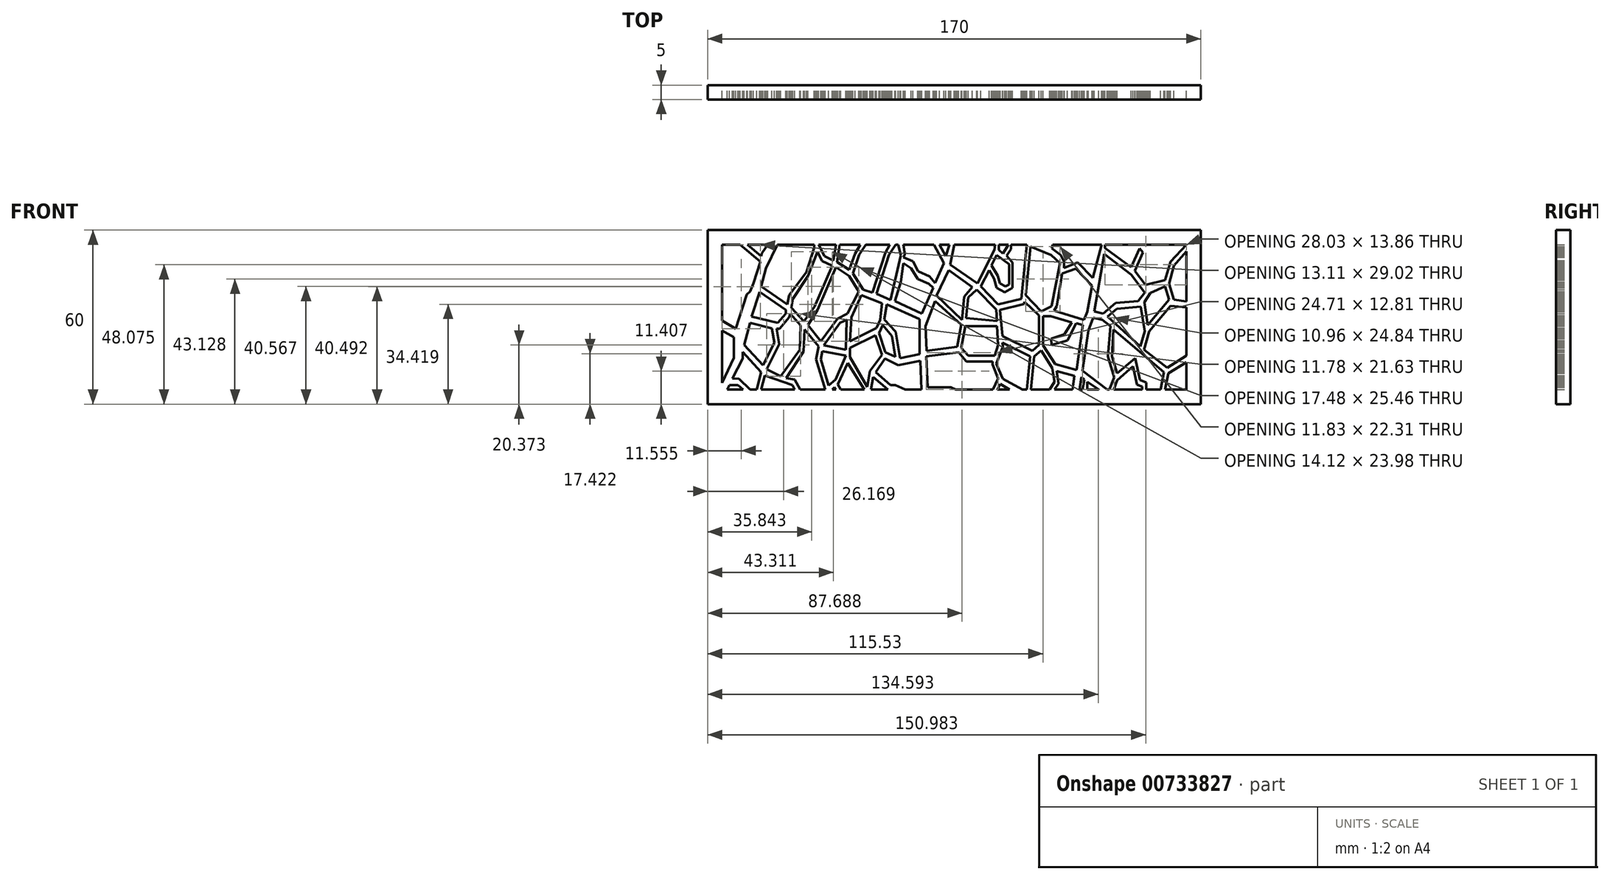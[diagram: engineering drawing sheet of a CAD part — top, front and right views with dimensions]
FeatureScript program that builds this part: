
annotation { "Feature Type Name" : "Feature", "Feature Type Description" : "" }
export const myFeature = defineFeature(function(context is Context, id is Id, definition is map)
    precondition{}
    {
        {
            var Q0;
            Q0=qCreatedBy(makeId("Front.planeOp"),FACE);
            var sketch = newSketch(context, id + "F0", { "sketchPlane" : qUnion([Q0])});
            skLineSegment(sketch, "E0.0", {"start": v(-29.57, -53.65) * mm, "end": v(130.43, -53.65) * mm});
            skLineSegment(sketch, "E0.1", {"start": v(-29.57, -103.65) * mm, "end": v(-29.57, -53.65) * mm});
            skLineSegment(sketch, "E0.2", {"start": v(130.43, -103.65) * mm, "end": v(-29.57, -103.65) * mm});
            skLineSegment(sketch, "E0.3", {"start": v(130.43, -103.65) * mm, "end": v(130.43, -53.65) * mm});
            skLineSegment(sketch, "E1", {"start": v(-29.57, -101.33) * mm, "end": v(-25.59, -92.68) * mm});
            skLineSegment(sketch, "E2", {"start": v(-25.59, -92.68) * mm, "end": v(-25.59, -85.56) * mm});
            skLineSegment(sketch, "E3", {"start": v(-25.59, -85.56) * mm, "end": v(-29.57, -83.34) * mm});
            skLineSegment(sketch, "E4", {"start": v(-27.87, -103.65) * mm, "end": v(-27.12, -102.02) * mm});
            skLineSegment(sketch, "E5", {"start": v(-27.12, -102.02) * mm, "end": v(-24.2, -102.02) * mm});
            skLineSegment(sketch, "E6", {"start": v(-24.2, -102.02) * mm, "end": v(-22.4, -103.65) * mm});
            skLineSegment(sketch, "E7", {"start": v(-26.07, -99.81) * mm, "end": v(-22.54, -92.9) * mm});
            skLineSegment(sketch, "E8", {"start": v(-22.54, -92.9) * mm, "end": v(-22.54, -90.6) * mm});
            skLineSegment(sketch, "E9", {"start": v(-22.54, -90.6) * mm, "end": v(-16.1, -97.6) * mm});
            skLineSegment(sketch, "E10", {"start": v(-16.1, -97.6) * mm, "end": v(-17.63, -103.65) * mm});
            skLineSegment(sketch, "E11", {"start": v(-19.91, -103.65) * mm, "end": v(-23.79, -99.88) * mm});
            skLineSegment(sketch, "E12", {"start": v(-23.79, -99.88) * mm, "end": v(-26.07, -99.81) * mm});
            skLineSegment(sketch, "E13", {"start": v(-22, -88.19) * mm, "end": v(-15.52, -95.21) * mm});
            skLineSegment(sketch, "E14", {"start": v(-15.52, -95.21) * mm, "end": v(-11.6, -87.53) * mm});
            skLineSegment(sketch, "E15", {"start": v(-11.6, -87.53) * mm, "end": v(-12.44, -82.51) * mm});
            skLineSegment(sketch, "E16", {"start": v(-12.44, -82.51) * mm, "end": v(-19.93, -80.63) * mm});
            skLineSegment(sketch, "E17", {"start": v(-19.93, -80.63) * mm, "end": v(-22, -88.19) * mm});
            skLineSegment(sketch, "E18", {"start": v(-16.1, -103.65) * mm, "end": v(-14.88, -98.77) * mm});
            skLineSegment(sketch, "E19", {"start": v(-14.88, -98.77) * mm, "end": v(-5.32, -102.02) * mm});
            skLineSegment(sketch, "E20", {"start": v(-5.32, -102.02) * mm, "end": v(-4.55, -103.65) * mm});
            skLineSegment(sketch, "E21", {"start": v(-6.15, -77.46) * mm, "end": v(-6.49, -78.68) * mm});
            skLineSegment(sketch, "E22", {"start": v(-6.49, -78.68) * mm, "end": v(-9.86, -82.67) * mm});
            skLineSegment(sketch, "E23", {"start": v(-9.86, -82.67) * mm, "end": v(-10.82, -82.67) * mm});
            skLineSegment(sketch, "E24", {"start": v(-10.82, -82.67) * mm, "end": v(-9.92, -87.93) * mm});
            skLineSegment(sketch, "E25", {"start": v(-9.92, -87.93) * mm, "end": v(-14.3, -96.68) * mm});
            skLineSegment(sketch, "E26", {"start": v(-14.3, -96.68) * mm, "end": v(-9.46, -99.1) * mm});
            skLineSegment(sketch, "E27", {"start": v(-9.46, -99.1) * mm, "end": v(-2.8, -89.9) * mm});
            skLineSegment(sketch, "E28", {"start": v(-2.8, -89.9) * mm, "end": v(-2.51, -81.56) * mm});
            skLineSegment(sketch, "E29", {"start": v(-2.51, -81.56) * mm, "end": v(-6.15, -77.46) * mm});
            skLineSegment(sketch, "E30", {"start": v(-1.11, -82.9) * mm, "end": v(3.69, -88.68) * mm});
            skLineSegment(sketch, "E31", {"start": v(3.69, -88.68) * mm, "end": v(2.81, -93.2) * mm});
            skLineSegment(sketch, "E32", {"start": v(2.81, -93.2) * mm, "end": v(5.94, -103.65) * mm});
            skLineSegment(sketch, "E33", {"start": v(-2.66, -103.65) * mm, "end": v(-4.6, -100.21) * mm});
            skLineSegment(sketch, "E34", {"start": v(-4.6, -100.21) * mm, "end": v(-7.51, -99.68) * mm});
            skLineSegment(sketch, "E35", {"start": v(-7.51, -99.68) * mm, "end": v(-1.53, -90.55) * mm});
            skLineSegment(sketch, "E36", {"start": v(-1.53, -90.55) * mm, "end": v(-1.11, -82.9) * mm});
            skLineSegment(sketch, "E37", {"start": v(7.09, -102.26) * mm, "end": v(4.38, -93.18) * mm});
            skPoint(sketch, "E37.endSnap0", {"position": v(4.38, -98.42) * mm});
            skLineSegment(sketch, "E38", {"start": v(4.38, -93.18) * mm, "end": v(4.9, -90.4) * mm});
            skLineSegment(sketch, "E39", {"start": v(4.9, -90.4) * mm, "end": v(13.02, -91.96) * mm});
            skLineSegment(sketch, "E40", {"start": v(13.02, -91.96) * mm, "end": v(9.52, -100.16) * mm});
            skLineSegment(sketch, "E41", {"start": v(9.52, -100.16) * mm, "end": v(7.09, -102.26) * mm});
            skLineSegment(sketch, "E42", {"start": v(8.3, -103.65) * mm, "end": v(9.16, -102.9) * mm});
            skPoint(sketch, "E42.startSnap0", {"position": v(8.3, -101.2) * mm});
            skLineSegment(sketch, "E43", {"start": v(9.16, -102.9) * mm, "end": v(9.58, -103.65) * mm});
            skLineSegment(sketch, "E44", {"start": v(11.34, -103.65) * mm, "end": v(10.29, -101.83) * mm});
            skLineSegment(sketch, "E45", {"start": v(10.29, -101.83) * mm, "end": v(13.64, -94.5) * mm});
            skLineSegment(sketch, "E46", {"start": v(13.64, -94.5) * mm, "end": v(19.36, -103.65) * mm});
            skLineSegment(sketch, "E47", {"start": v(20.49, -102.69) * mm, "end": v(14.45, -92.42) * mm});
            skLineSegment(sketch, "E48", {"start": v(14.45, -92.42) * mm, "end": v(14.45, -89.3) * mm});
            skLineSegment(sketch, "E49", {"start": v(14.45, -89.3) * mm, "end": v(23.18, -84.96) * mm});
            skLineSegment(sketch, "E50", {"start": v(23.18, -84.96) * mm, "end": v(25.5, -91.66) * mm});
            skLineSegment(sketch, "E51", {"start": v(25.5, -91.66) * mm, "end": v(21.32, -97.28) * mm});
            skLineSegment(sketch, "E52", {"start": v(21.32, -97.28) * mm, "end": v(20.49, -102.69) * mm});
            skLineSegment(sketch, "E53", {"start": v(5.46, -88.33) * mm, "end": v(13.07, -89.85) * mm});
            skLineSegment(sketch, "E54", {"start": v(13.07, -89.85) * mm, "end": v(13.29, -79.56) * mm});
            skLineSegment(sketch, "E55", {"start": v(13.29, -79.56) * mm, "end": v(11.06, -80.67) * mm});
            skLineSegment(sketch, "E56", {"start": v(11.06, -80.67) * mm, "end": v(5.46, -88.33) * mm});
            skLineSegment(sketch, "E57", {"start": v(4.44, -86.96) * mm, "end": v(10.14, -79.16) * mm});
            skLineSegment(sketch, "E58", {"start": v(10.14, -79.16) * mm, "end": v(13.59, -77.44) * mm});
            skLineSegment(sketch, "E59", {"start": v(13.59, -77.44) * mm, "end": v(17.48, -69.77) * mm});
            skLineSegment(sketch, "E60", {"start": v(17.48, -69.77) * mm, "end": v(14.17, -64.47) * mm});
            skLineSegment(sketch, "E61", {"start": v(14.17, -64.47) * mm, "end": v(9.65, -61.5) * mm});
            skLineSegment(sketch, "E62", {"start": v(9.65, -61.5) * mm, "end": v(3.33, -76.24) * mm});
            skLineSegment(sketch, "E63", {"start": v(3.33, -76.24) * mm, "end": v(0, -81.32) * mm});
            skLineSegment(sketch, "E64", {"start": v(0, -81.32) * mm, "end": v(4.44, -86.96) * mm});
            skLineSegment(sketch, "E65", {"start": v(14.45, -86.96) * mm, "end": v(23.64, -82.38) * mm});
            skLineSegment(sketch, "E66", {"start": v(23.64, -82.38) * mm, "end": v(24.92, -79.56) * mm});
            skLineSegment(sketch, "E67", {"start": v(24.92, -79.56) * mm, "end": v(25.5, -73.83) * mm});
            skLineSegment(sketch, "E68", {"start": v(25.5, -73.83) * mm, "end": v(18.42, -71.1) * mm});
            skLineSegment(sketch, "E69", {"start": v(18.42, -71.1) * mm, "end": v(14.94, -78.72) * mm});
            skLineSegment(sketch, "E70", {"start": v(14.94, -78.72) * mm, "end": v(14.45, -86.96) * mm});
            skLineSegment(sketch, "E71", {"start": v(8.33, -60.96) * mm, "end": v(2.29, -75.06) * mm});
            skLineSegment(sketch, "E72", {"start": v(2.29, -75.06) * mm, "end": v(-1.37, -80.07) * mm});
            skLineSegment(sketch, "E73", {"start": v(-1.37, -80.07) * mm, "end": v(-5.79, -75.45) * mm});
            skLineSegment(sketch, "E74", {"start": v(-5.79, -75.45) * mm, "end": v(-5.16, -72.34) * mm});
            skLineSegment(sketch, "E75", {"start": v(-5.16, -72.34) * mm, "end": v(0, -64.46) * mm});
            skLineSegment(sketch, "E76", {"start": v(0, -64.46) * mm, "end": v(3.23, -56.1) * mm});
            skLineSegment(sketch, "E77", {"start": v(3.23, -56.1) * mm, "end": v(4.8, -59.26) * mm});
            skLineSegment(sketch, "E78", {"start": v(4.8, -59.26) * mm, "end": v(8.33, -60.96) * mm});
            skLineSegment(sketch, "E79", {"start": v(-19.43, -78.5) * mm, "end": v(-10.37, -80.67) * mm});
            skLineSegment(sketch, "E80", {"start": v(-10.37, -80.67) * mm, "end": v(-7.66, -77.46) * mm});
            skLineSegment(sketch, "E81", {"start": v(-7.66, -77.46) * mm, "end": v(-7.66, -76.24) * mm});
            skLineSegment(sketch, "E82", {"start": v(-7.66, -76.24) * mm, "end": v(-16.71, -70) * mm});
            skLineSegment(sketch, "E83", {"start": v(-16.71, -70) * mm, "end": v(-19.43, -78.5) * mm});
            skLineSegment(sketch, "E84", {"start": v(-29.57, -79.81) * mm, "end": v(-24.9, -82.67) * mm});
            skLineSegment(sketch, "E85", {"start": v(-24.9, -82.67) * mm, "end": v(-21.12, -70.83) * mm});
            skLineSegment(sketch, "E86", {"start": v(-21.12, -70.83) * mm, "end": v(-20.01, -69.77) * mm});
            skLineSegment(sketch, "E87", {"start": v(-20.01, -69.77) * mm, "end": v(-18.86, -67.08) * mm});
            skLineSegment(sketch, "E88", {"start": v(-18.86, -67.08) * mm, "end": v(-16.46, -59.54) * mm});
            skLineSegment(sketch, "E89", {"start": v(-16.46, -59.54) * mm, "end": v(-23.42, -53.65) * mm});
            skLineSegment(sketch, "E90", {"start": v(-20.84, -53.65) * mm, "end": v(-16.11, -57.65) * mm});
            skLineSegment(sketch, "E91", {"start": v(-16.11, -57.65) * mm, "end": v(-15.84, -56.62) * mm});
            skLineSegment(sketch, "E92", {"start": v(-15.84, -56.62) * mm, "end": v(-13.82, -53.65) * mm});
            skLineSegment(sketch, "E93", {"start": v(-10.58, -53.65) * mm, "end": v(-14.44, -61.83) * mm});
            skLineSegment(sketch, "E94", {"start": v(-14.44, -61.83) * mm, "end": v(-16.2, -68.05) * mm});
            skLineSegment(sketch, "E95", {"start": v(-16.2, -68.05) * mm, "end": v(-7.07, -74.23) * mm});
            skLineSegment(sketch, "E96", {"start": v(-7.07, -74.23) * mm, "end": v(-6.48, -71.12) * mm});
            skLineSegment(sketch, "E97", {"start": v(-6.48, -71.12) * mm, "end": v(-0.58, -63.05) * mm});
            skLineSegment(sketch, "E98", {"start": v(-0.58, -63.05) * mm, "end": v(2.18, -54.71) * mm});
            skLineSegment(sketch, "E99", {"start": v(21.74, -103.65) * mm, "end": v(22.41, -99.31) * mm});
            skLineSegment(sketch, "E100", {"start": v(22.41, -99.31) * mm, "end": v(27.6, -103.65) * mm});
            skLineSegment(sketch, "E101", {"start": v(26.57, -93) * mm, "end": v(23.36, -97.64) * mm});
            skLineSegment(sketch, "E102", {"start": v(23.36, -97.64) * mm, "end": v(28.39, -102.05) * mm});
            skLineSegment(sketch, "E103", {"start": v(28.39, -102.05) * mm, "end": v(30.08, -102.05) * mm});
            skLineSegment(sketch, "E104", {"start": v(30.08, -102.05) * mm, "end": v(33.45, -103.65) * mm});
            skLineSegment(sketch, "E105", {"start": v(26.57, -93) * mm, "end": v(31.08, -95.2) * mm});
            skLineSegment(sketch, "E106", {"start": v(31.08, -95.2) * mm, "end": v(38.77, -93.67) * mm});
            skLineSegment(sketch, "E107", {"start": v(38.77, -93.67) * mm, "end": v(39.07, -103.65) * mm});
            skLineSegment(sketch, "E108", {"start": v(25.74, -81.4) * mm, "end": v(24.5, -84.14) * mm});
            skLineSegment(sketch, "E109", {"start": v(24.5, -84.14) * mm, "end": v(26.71, -90.82) * mm});
            skLineSegment(sketch, "E110", {"start": v(26.71, -90.82) * mm, "end": v(30.03, -92.33) * mm});
            skLineSegment(sketch, "E111", {"start": v(30.03, -92.33) * mm, "end": v(28.99, -85.13) * mm});
            skLineSegment(sketch, "E112", {"start": v(28.99, -85.13) * mm, "end": v(25.74, -81.4) * mm});
            skLineSegment(sketch, "E113", {"start": v(27.1, -74.33) * mm, "end": v(26.3, -79.51) * mm});
            skLineSegment(sketch, "E114", {"start": v(26.3, -79.51) * mm, "end": v(30.16, -83.64) * mm});
            skLineSegment(sketch, "E115", {"start": v(30.16, -83.64) * mm, "end": v(31.71, -92.8) * mm});
            skLineSegment(sketch, "E116", {"start": v(31.71, -92.8) * mm, "end": v(38.52, -91.45) * mm});
            skLineSegment(sketch, "E117", {"start": v(38.52, -91.45) * mm, "end": v(38.52, -79.32) * mm});
            skLineSegment(sketch, "E118", {"start": v(38.52, -79.32) * mm, "end": v(27.1, -74.33) * mm});
            skLineSegment(sketch, "E119", {"start": v(40.76, -92.23) * mm, "end": v(41.3, -102.88) * mm});
            skLineSegment(sketch, "E120", {"start": v(41.3, -102.88) * mm, "end": v(49.22, -102.88) * mm});
            skLineSegment(sketch, "E121", {"start": v(49.22, -102.88) * mm, "end": v(50.9, -103.65) * mm});
            skLineSegment(sketch, "E122", {"start": v(40.76, -92.23) * mm, "end": v(51.88, -90.84) * mm});
            skLineSegment(sketch, "E123", {"start": v(51.88, -90.84) * mm, "end": v(54.64, -94) * mm});
            skLineSegment(sketch, "E124", {"start": v(54.64, -94) * mm, "end": v(63.65, -94) * mm});
            skLineSegment(sketch, "E125", {"start": v(63.65, -94) * mm, "end": v(63.65, -94.97) * mm});
            skLineSegment(sketch, "E126", {"start": v(63.65, -94.97) * mm, "end": v(65.47, -99.74) * mm});
            skLineSegment(sketch, "E127", {"start": v(65.47, -99.74) * mm, "end": v(63.7, -103.65) * mm});
            skLineSegment(sketch, "E128", {"start": v(40.81, -90.23) * mm, "end": v(51.43, -88.9) * mm});
            skLineSegment(sketch, "E129", {"start": v(51.43, -88.9) * mm, "end": v(52.87, -81.26) * mm});
            skLineSegment(sketch, "E130", {"start": v(52.87, -81.26) * mm, "end": v(43.74, -73.17) * mm});
            skLineSegment(sketch, "E131", {"start": v(43.74, -73.17) * mm, "end": v(40.51, -81.73) * mm});
            skLineSegment(sketch, "E132", {"start": v(40.51, -81.73) * mm, "end": v(40.81, -90.23) * mm});
            skLineSegment(sketch, "E133", {"start": v(52.87, -89.23) * mm, "end": v(55.22, -91.92) * mm});
            skLineSegment(sketch, "E134", {"start": v(55.22, -91.92) * mm, "end": v(64.36, -91.92) * mm});
            skLineSegment(sketch, "E135", {"start": v(64.36, -91.92) * mm, "end": v(65.56, -88.3) * mm});
            skLineSegment(sketch, "E136", {"start": v(65.56, -88.3) * mm, "end": v(65.12, -81.75) * mm});
            skLineSegment(sketch, "E137", {"start": v(65.12, -81.75) * mm, "end": v(56.8, -81.75) * mm});
            skLineSegment(sketch, "E138", {"start": v(56.8, -81.75) * mm, "end": v(54.16, -81.75) * mm});
            skLineSegment(sketch, "E139", {"start": v(54.16, -81.75) * mm, "end": v(52.87, -89.23) * mm});
            skLineSegment(sketch, "E140", {"start": v(67, -87.47) * mm, "end": v(67.1, -88.9) * mm});
            skLineSegment(sketch, "E141", {"start": v(67.1, -88.9) * mm, "end": v(64.89, -94.73) * mm});
            skLineSegment(sketch, "E142", {"start": v(64.89, -94.73) * mm, "end": v(67.1, -99.9) * mm});
            skLineSegment(sketch, "E143", {"start": v(67.1, -99.9) * mm, "end": v(73.9, -103.65) * mm});
            skLineSegment(sketch, "E144", {"start": v(75.4, -103.65) * mm, "end": v(76.6, -92.14) * mm});
            skLineSegment(sketch, "E145", {"start": v(76.6, -92.14) * mm, "end": v(67, -87.47) * mm});
            skLineSegment(sketch, "E146", {"start": v(67, -85.18) * mm, "end": v(77.36, -90.21) * mm});
            skLineSegment(sketch, "E147", {"start": v(77.36, -90.21) * mm, "end": v(79.57, -88.28) * mm});
            skLineSegment(sketch, "E148", {"start": v(79.57, -88.28) * mm, "end": v(79.57, -78.09) * mm});
            skLineSegment(sketch, "E149", {"start": v(79.57, -78.09) * mm, "end": v(74.65, -73.33) * mm});
            skLineSegment(sketch, "E150", {"start": v(74.65, -73.33) * mm, "end": v(74.46, -74.2) * mm});
            skLineSegment(sketch, "E151", {"start": v(74.46, -74.2) * mm, "end": v(66.12, -76.23) * mm});
            skLineSegment(sketch, "E152", {"start": v(66.12, -76.23) * mm, "end": v(67, -85.18) * mm});
            skLineSegment(sketch, "E153", {"start": v(44.35, -71.2) * mm, "end": v(53.02, -79.6) * mm});
            skLineSegment(sketch, "E154", {"start": v(53.02, -79.6) * mm, "end": v(53.77, -71.57) * mm});
            skLineSegment(sketch, "E155", {"start": v(53.77, -71.57) * mm, "end": v(56.68, -68.29) * mm});
            skLineSegment(sketch, "E156", {"start": v(56.68, -68.29) * mm, "end": v(48.54, -62.48) * mm});
            skLineSegment(sketch, "E157", {"start": v(48.54, -62.48) * mm, "end": v(44.35, -71.2) * mm});
            skLineSegment(sketch, "E158", {"start": v(58.17, -69.18) * mm, "end": v(55.19, -71.8) * mm});
            skLineSegment(sketch, "E159", {"start": v(55.19, -71.8) * mm, "end": v(54.51, -79) * mm});
            skLineSegment(sketch, "E160", {"start": v(54.51, -79) * mm, "end": v(65.12, -79.99) * mm});
            skLineSegment(sketch, "E161", {"start": v(65.12, -79.99) * mm, "end": v(64.86, -76.06) * mm});
            skLineSegment(sketch, "E162", {"start": v(64.86, -76.06) * mm, "end": v(58.17, -69.18) * mm});
            skLineSegment(sketch, "E163", {"start": v(65.27, -103.65) * mm, "end": v(66.22, -101.7) * mm});
            skLineSegment(sketch, "E164", {"start": v(66.22, -101.7) * mm, "end": v(69.49, -103.65) * mm});
            skLineSegment(sketch, "E165", {"start": v(3.66, -53.65) * mm, "end": v(5.72, -57.64) * mm});
            skLineSegment(sketch, "E166", {"start": v(5.72, -57.64) * mm, "end": v(8.72, -59.12) * mm});
            skLineSegment(sketch, "E167", {"start": v(8.72, -59.12) * mm, "end": v(9.63, -53.65) * mm});
            skLineSegment(sketch, "E168", {"start": v(10.86, -53.65) * mm, "end": v(10, -59.62) * mm});
            skLineSegment(sketch, "E169", {"start": v(10, -59.62) * mm, "end": v(14.16, -62.38) * mm});
            skLineSegment(sketch, "E170", {"start": v(14.16, -62.38) * mm, "end": v(16.17, -56.7) * mm});
            skLineSegment(sketch, "E171", {"start": v(16.17, -56.7) * mm, "end": v(17.98, -53.65) * mm});
            skLineSegment(sketch, "E172", {"start": v(19.92, -53.65) * mm, "end": v(17.57, -57.07) * mm});
            skLineSegment(sketch, "E173", {"start": v(17.57, -57.07) * mm, "end": v(15.44, -63.66) * mm});
            skLineSegment(sketch, "E174", {"start": v(15.44, -63.66) * mm, "end": v(18.98, -69.22) * mm});
            skLineSegment(sketch, "E175", {"start": v(18.98, -69.22) * mm, "end": v(22.2, -70.25) * mm});
            skLineSegment(sketch, "E176", {"start": v(22.2, -70.25) * mm, "end": v(26.63, -56.45) * mm});
            skLineSegment(sketch, "E177", {"start": v(26.63, -56.45) * mm, "end": v(28.15, -53.65) * mm});
            skLineSegment(sketch, "E178", {"start": v(30.25, -53.65) * mm, "end": v(27.93, -57.15) * mm});
            skLineSegment(sketch, "E179", {"start": v(27.93, -57.15) * mm, "end": v(23.62, -70.57) * mm});
            skLineSegment(sketch, "E180", {"start": v(23.62, -70.57) * mm, "end": v(28.45, -72.77) * mm});
            skLineSegment(sketch, "E181", {"start": v(28.45, -72.77) * mm, "end": v(31.98, -57.42) * mm});
            skLineSegment(sketch, "E182", {"start": v(31.98, -57.42) * mm, "end": v(31.08, -53.65) * mm});
            skLineSegment(sketch, "E183", {"start": v(32.93, -60.05) * mm, "end": v(31.95, -66.47) * mm});
            skLineSegment(sketch, "E184", {"start": v(31.95, -66.47) * mm, "end": v(29.9, -73.17) * mm});
            skLineSegment(sketch, "E185", {"start": v(29.9, -73.17) * mm, "end": v(39.17, -77.4) * mm});
            skLineSegment(sketch, "E186", {"start": v(39.17, -77.4) * mm, "end": v(43.2, -68.54) * mm});
            skLineSegment(sketch, "E187", {"start": v(43.2, -68.54) * mm, "end": v(41.6, -67.14) * mm});
            skLineSegment(sketch, "E188", {"start": v(41.6, -67.14) * mm, "end": v(37.78, -65.47) * mm});
            skLineSegment(sketch, "E189", {"start": v(37.78, -65.47) * mm, "end": v(35.55, -61.85) * mm});
            skLineSegment(sketch, "E190", {"start": v(35.55, -61.85) * mm, "end": v(32.93, -60.05) * mm});
            skLineSegment(sketch, "E191", {"start": v(32.93, -58) * mm, "end": v(36.23, -59.45) * mm});
            skLineSegment(sketch, "E192", {"start": v(36.23, -59.45) * mm, "end": v(37.94, -62.84) * mm});
            skLineSegment(sketch, "E193", {"start": v(37.94, -62.84) * mm, "end": v(41.9, -64.56) * mm});
            skLineSegment(sketch, "E194", {"start": v(41.9, -64.56) * mm, "end": v(43.82, -66.85) * mm});
            skLineSegment(sketch, "E195", {"start": v(43.82, -66.85) * mm, "end": v(46.78, -60.05) * mm});
            skLineSegment(sketch, "E196", {"start": v(46.78, -60.05) * mm, "end": v(43.41, -53.65) * mm});
            skLineSegment(sketch, "E197", {"start": v(32.93, -58) * mm, "end": v(33.35, -57.05) * mm});
            skLineSegment(sketch, "E198", {"start": v(33.35, -57.05) * mm, "end": v(32.93, -53.65) * mm});
            skLineSegment(sketch, "E199", {"start": v(45.26, -53.65) * mm, "end": v(47.42, -57.6) * mm});
            skLineSegment(sketch, "E200", {"start": v(47.42, -57.6) * mm, "end": v(48.7, -53.65) * mm});
            skLineSegment(sketch, "E201", {"start": v(50.43, -53.65) * mm, "end": v(49.05, -60.52) * mm});
            skLineSegment(sketch, "E202", {"start": v(49.05, -60.52) * mm, "end": v(58.38, -67.05) * mm});
            skLineSegment(sketch, "E203", {"start": v(58.38, -67.05) * mm, "end": v(64.23, -55.49) * mm});
            skLineSegment(sketch, "E204", {"start": v(64.23, -55.49) * mm, "end": v(64.53, -53.65) * mm});
            skLineSegment(sketch, "E205", {"start": v(65.82, -53.65) * mm, "end": v(65.82, -55.43) * mm});
            skLineSegment(sketch, "E206", {"start": v(65.82, -55.43) * mm, "end": v(67.2, -56.73) * mm});
            skLineSegment(sketch, "E207", {"start": v(67.2, -56.73) * mm, "end": v(69.1, -53.65) * mm});
            skLineSegment(sketch, "E208", {"start": v(59.56, -67.98) * mm, "end": v(65.5, -74.22) * mm});
            skLineSegment(sketch, "E209", {"start": v(65.5, -74.22) * mm, "end": v(73.52, -72.36) * mm});
            skLineSegment(sketch, "E210", {"start": v(73.52, -72.36) * mm, "end": v(75.36, -53.65) * mm});
            skLineSegment(sketch, "E211", {"start": v(59.56, -67.98) * mm, "end": v(62.47, -62.5) * mm});
            skLineSegment(sketch, "E212", {"start": v(62.47, -62.5) * mm, "end": v(64.06, -65.36) * mm});
            skLineSegment(sketch, "E213", {"start": v(64.06, -65.36) * mm, "end": v(65, -68.53) * mm});
            skLineSegment(sketch, "E214", {"start": v(65, -68.53) * mm, "end": v(67.76, -70.1) * mm});
            skLineSegment(sketch, "E215", {"start": v(67.76, -70.1) * mm, "end": v(70.52, -68.59) * mm});
            skLineSegment(sketch, "E216", {"start": v(70.52, -68.59) * mm, "end": v(70.52, -59.77) * mm});
            skLineSegment(sketch, "E217", {"start": v(70.52, -59.77) * mm, "end": v(68.44, -57.49) * mm});
            skLineSegment(sketch, "E218", {"start": v(68.44, -57.49) * mm, "end": v(69.98, -55.2) * mm});
            skLineSegment(sketch, "E219", {"start": v(69.98, -55.2) * mm, "end": v(69.98, -53.65) * mm});
            skLineSegment(sketch, "E220", {"start": v(64.95, -57.28) * mm, "end": v(63.27, -60.8) * mm});
            skLineSegment(sketch, "E221", {"start": v(63.27, -60.8) * mm, "end": v(65.37, -64.4) * mm});
            skLineSegment(sketch, "E222", {"start": v(65.37, -64.4) * mm, "end": v(66.09, -66.99) * mm});
            skLineSegment(sketch, "E223", {"start": v(66.09, -66.99) * mm, "end": v(68.1, -68.08) * mm});
            skLineSegment(sketch, "E224", {"start": v(68.1, -68.08) * mm, "end": v(69.3, -67.37) * mm});
            skLineSegment(sketch, "E225", {"start": v(69.3, -67.37) * mm, "end": v(69.3, -60.48) * mm});
            skLineSegment(sketch, "E226", {"start": v(69.3, -60.48) * mm, "end": v(64.95, -57.28) * mm});
            skLineSegment(sketch, "E227", {"start": v(76.77, -103.65) * mm, "end": v(77.9, -92.12) * mm});
            skLineSegment(sketch, "E228", {"start": v(77.9, -92.12) * mm, "end": v(80.33, -90.08) * mm});
            skLineSegment(sketch, "E229", {"start": v(80.33, -90.08) * mm, "end": v(84.15, -96.21) * mm});
            skLineSegment(sketch, "E230", {"start": v(84.15, -96.21) * mm, "end": v(84.98, -100.96) * mm});
            skLineSegment(sketch, "E231", {"start": v(84.98, -100.96) * mm, "end": v(83.25, -103.65) * mm});
            skLineSegment(sketch, "E232", {"start": v(84.98, -103.65) * mm, "end": v(86.33, -101.54) * mm});
            skLineSegment(sketch, "E233", {"start": v(86.33, -101.54) * mm, "end": v(85.65, -97.23) * mm});
            skLineSegment(sketch, "E234", {"start": v(85.65, -97.23) * mm, "end": v(91.86, -98.97) * mm});
            skLineSegment(sketch, "E235", {"start": v(91.86, -98.97) * mm, "end": v(91.1, -103.65) * mm});
            skLineSegment(sketch, "E236", {"start": v(93.57, -103.65) * mm, "end": v(94.24, -99.33) * mm});
            skLineSegment(sketch, "E237", {"start": v(94.24, -99.33) * mm, "end": v(95.29, -100.15) * mm});
            skLineSegment(sketch, "E238", {"start": v(95.29, -100.15) * mm, "end": v(94.56, -103.65) * mm});
            skLineSegment(sketch, "E239", {"start": v(96.2, -103.65) * mm, "end": v(96.2, -100.97) * mm});
            skLineSegment(sketch, "E240", {"start": v(96.2, -100.97) * mm, "end": v(100.2, -103.65) * mm});
            skLineSegment(sketch, "E241", {"start": v(103.16, -103.65) * mm, "end": v(94.54, -97.13) * mm});
            skLineSegment(sketch, "E242", {"start": v(94.54, -97.13) * mm, "end": v(96.66, -83.33) * mm});
            skLineSegment(sketch, "E243", {"start": v(96.66, -83.33) * mm, "end": v(98.3, -78.8) * mm});
            skLineSegment(sketch, "E244", {"start": v(98.3, -78.8) * mm, "end": v(101.48, -79.56) * mm});
            skLineSegment(sketch, "E245", {"start": v(101.48, -79.56) * mm, "end": v(104.19, -81.78) * mm});
            skLineSegment(sketch, "E246", {"start": v(104.19, -81.78) * mm, "end": v(103.34, -92.18) * mm});
            skLineSegment(sketch, "E247", {"start": v(103.34, -92.18) * mm, "end": v(105.5, -99.4) * mm});
            skLineSegment(sketch, "E248", {"start": v(105.5, -99.4) * mm, "end": v(103.85, -103.65) * mm});
            skLineSegment(sketch, "E249", {"start": v(105.43, -103.65) * mm, "end": v(106.56, -100.42) * mm});
            skLineSegment(sketch, "E250", {"start": v(106.56, -100.42) * mm, "end": v(111.96, -95.66) * mm});
            skLineSegment(sketch, "E251", {"start": v(111.96, -95.66) * mm, "end": v(113.4, -102) * mm});
            skLineSegment(sketch, "E252", {"start": v(113.4, -102) * mm, "end": v(115.15, -102.58) * mm});
            skLineSegment(sketch, "E253", {"start": v(115.15, -102.58) * mm, "end": v(115.15, -103.65) * mm});
            skLineSegment(sketch, "E254", {"start": v(116.55, -103.65) * mm, "end": v(116.55, -101.14) * mm});
            skLineSegment(sketch, "E255", {"start": v(116.55, -101.14) * mm, "end": v(114.46, -100.28) * mm});
            skLineSegment(sketch, "E256", {"start": v(114.46, -100.28) * mm, "end": v(112.8, -92.76) * mm});
            skLineSegment(sketch, "E257", {"start": v(112.8, -92.76) * mm, "end": v(106.56, -97.97) * mm});
            skLineSegment(sketch, "E258", {"start": v(106.56, -97.97) * mm, "end": v(104.78, -92.11) * mm});
            skLineSegment(sketch, "E259", {"start": v(104.78, -92.11) * mm, "end": v(105.3, -82.9) * mm});
            skLineSegment(sketch, "E260", {"start": v(105.3, -82.9) * mm, "end": v(122.72, -97.6) * mm});
            skLineSegment(sketch, "E261", {"start": v(122.72, -97.6) * mm, "end": v(121.54, -103.65) * mm});
            skLineSegment(sketch, "E262", {"start": v(123.07, -103.65) * mm, "end": v(124.2, -97.97) * mm});
            skLineSegment(sketch, "E263", {"start": v(124.2, -97.97) * mm, "end": v(130.43, -94.18) * mm});
            skLineSegment(sketch, "E264", {"start": v(130.43, -91.92) * mm, "end": v(123.87, -96.06) * mm});
            skLineSegment(sketch, "E265", {"start": v(123.87, -96.06) * mm, "end": v(115.85, -89.93) * mm});
            skLineSegment(sketch, "E266", {"start": v(115.85, -89.93) * mm, "end": v(117.62, -83.53) * mm});
            skLineSegment(sketch, "E267", {"start": v(117.62, -83.53) * mm, "end": v(125.01, -74.8) * mm});
            skLineSegment(sketch, "E268", {"start": v(125.01, -74.8) * mm, "end": v(130.43, -75.26) * mm});
            skLineSegment(sketch, "E269", {"start": v(103.2, -78.5) * mm, "end": v(114.54, -88.78) * mm});
            skLineSegment(sketch, "E270", {"start": v(114.54, -88.78) * mm, "end": v(116.1, -83.53) * mm});
            skLineSegment(sketch, "E271", {"start": v(116.1, -83.53) * mm, "end": v(114.7, -75) * mm});
            skLineSegment(sketch, "E272", {"start": v(114.7, -75) * mm, "end": v(106.4, -75.78) * mm});
            skLineSegment(sketch, "E273", {"start": v(106.4, -75.78) * mm, "end": v(103.2, -78.5) * mm});
            skLineSegment(sketch, "E274", {"start": v(123.05, -68) * mm, "end": v(117.93, -70.33) * mm});
            skLineSegment(sketch, "E275", {"start": v(117.93, -70.33) * mm, "end": v(115.9, -73.46) * mm});
            skLineSegment(sketch, "E276", {"start": v(115.9, -73.46) * mm, "end": v(117.05, -81.4) * mm});
            skLineSegment(sketch, "E277", {"start": v(117.05, -81.4) * mm, "end": v(124.5, -72.62) * mm});
            skLineSegment(sketch, "E278", {"start": v(124.5, -72.62) * mm, "end": v(123.05, -68) * mm});
            skLineSegment(sketch, "E279", {"start": v(130.43, -73.2) * mm, "end": v(126.06, -72.62) * mm});
            skLineSegment(sketch, "E280", {"start": v(126.06, -72.62) * mm, "end": v(124.5, -67.14) * mm});
            skLineSegment(sketch, "E281", {"start": v(124.5, -67.14) * mm, "end": v(126.15, -60.96) * mm});
            skLineSegment(sketch, "E282", {"start": v(126.15, -60.96) * mm, "end": v(130.43, -55.92) * mm});
            skLineSegment(sketch, "E283", {"start": v(130.43, -53.65) * mm, "end": v(124.97, -59.5) * mm});
            skLineSegment(sketch, "E284", {"start": v(124.97, -59.5) * mm, "end": v(123.08, -65.93) * mm});
            skLineSegment(sketch, "E285", {"start": v(123.08, -65.93) * mm, "end": v(116.37, -67.5) * mm});
            skLineSegment(sketch, "E286", {"start": v(116.37, -67.5) * mm, "end": v(112.67, -62.74) * mm});
            skLineSegment(sketch, "E287", {"start": v(112.67, -62.74) * mm, "end": v(115.39, -56.36) * mm});
            skLineSegment(sketch, "E288", {"start": v(115.39, -56.36) * mm, "end": v(114.25, -55.03) * mm});
            skLineSegment(sketch, "E289", {"start": v(114.25, -55.03) * mm, "end": v(111.33, -61.49) * mm});
            skLineSegment(sketch, "E290", {"start": v(111.33, -61.49) * mm, "end": v(102.4, -54.8) * mm});
            skLineSegment(sketch, "E291", {"start": v(102.4, -54.8) * mm, "end": v(102.4, -53.65) * mm});
            skLineSegment(sketch, "E292", {"start": v(114.2, -53.65) * mm, "end": v(115.66, -55.2) * mm});
            skLineSegment(sketch, "E293", {"start": v(115.66, -55.2) * mm, "end": v(120.59, -56.12) * mm});
            skLineSegment(sketch, "E294", {"start": v(120.59, -56.12) * mm, "end": v(121.96, -53.65) * mm});
            skLineSegment(sketch, "E295", {"start": v(102.03, -56.89) * mm, "end": v(111.36, -63.95) * mm});
            skLineSegment(sketch, "E296", {"start": v(111.36, -63.95) * mm, "end": v(116.12, -70.15) * mm});
            skLineSegment(sketch, "E297", {"start": v(116.12, -70.15) * mm, "end": v(113.82, -73.12) * mm});
            skLineSegment(sketch, "E298", {"start": v(113.82, -73.12) * mm, "end": v(105.97, -73.73) * mm});
            skLineSegment(sketch, "E299", {"start": v(105.97, -73.73) * mm, "end": v(101.7, -77.5) * mm});
            skLineSegment(sketch, "E300", {"start": v(101.7, -77.5) * mm, "end": v(98.63, -76.68) * mm});
            skLineSegment(sketch, "E301", {"start": v(98.63, -76.68) * mm, "end": v(102.03, -56.89) * mm});
            skLineSegment(sketch, "E302", {"start": v(101.18, -53.65) * mm, "end": v(98.1, -65.15) * mm});
            skLineSegment(sketch, "E303", {"start": v(98.1, -65.15) * mm, "end": v(92.97, -59.83) * mm});
            skLineSegment(sketch, "E304", {"start": v(92.97, -59.83) * mm, "end": v(88.23, -61.66) * mm});
            skLineSegment(sketch, "E305", {"start": v(88.23, -61.66) * mm, "end": v(88.23, -59.52) * mm});
            skLineSegment(sketch, "E306", {"start": v(88.23, -59.52) * mm, "end": v(87.09, -57.24) * mm});
            skLineSegment(sketch, "E307", {"start": v(87.09, -57.24) * mm, "end": v(84, -54.91) * mm});
            skLineSegment(sketch, "E308", {"start": v(84, -54.91) * mm, "end": v(84.35, -53.65) * mm});
            skLineSegment(sketch, "E309", {"start": v(87.57, -63.64) * mm, "end": v(92.3, -62) * mm});
            skLineSegment(sketch, "E310", {"start": v(92.3, -62) * mm, "end": v(97.85, -67.77) * mm});
            skLineSegment(sketch, "E311", {"start": v(97.85, -67.77) * mm, "end": v(96.3, -76.78) * mm});
            skLineSegment(sketch, "E312", {"start": v(96.3, -76.78) * mm, "end": v(95.15, -79.58) * mm});
            skLineSegment(sketch, "E313", {"start": v(95.15, -79.58) * mm, "end": v(84.8, -76.49) * mm});
            skLineSegment(sketch, "E314", {"start": v(84.8, -76.49) * mm, "end": v(85.76, -74.9) * mm});
            skLineSegment(sketch, "E315", {"start": v(85.76, -74.9) * mm, "end": v(87.57, -63.64) * mm});
            skLineSegment(sketch, "E316", {"start": v(94.7, -81.42) * mm, "end": v(92.55, -96.85) * mm});
            skLineSegment(sketch, "E317", {"start": v(92.55, -96.85) * mm, "end": v(85.22, -94.87) * mm});
            skLineSegment(sketch, "E318", {"start": v(85.22, -94.87) * mm, "end": v(80.97, -88.41) * mm});
            skLineSegment(sketch, "E319", {"start": v(80.97, -88.41) * mm, "end": v(80.97, -78.38) * mm});
            skLineSegment(sketch, "E320", {"start": v(80.97, -78.38) * mm, "end": v(83.74, -78.38) * mm});
            skLineSegment(sketch, "E321", {"start": v(83.74, -78.38) * mm, "end": v(90.86, -80.43) * mm});
            skLineSegment(sketch, "E322", {"start": v(90.86, -80.43) * mm, "end": v(88.42, -84.57) * mm});
            skLineSegment(sketch, "E323", {"start": v(88.42, -84.57) * mm, "end": v(83.78, -86.03) * mm});
            skLineSegment(sketch, "E324", {"start": v(83.78, -86.03) * mm, "end": v(83.88, -88.28) * mm});
            skLineSegment(sketch, "E325", {"start": v(83.88, -88.28) * mm, "end": v(89.35, -86.74) * mm});
            skLineSegment(sketch, "E326", {"start": v(89.35, -86.74) * mm, "end": v(92.46, -80.78) * mm});
            skLineSegment(sketch, "E327", {"start": v(92.46, -80.78) * mm, "end": v(94.7, -81.42) * mm});
            skLineSegment(sketch, "E328", {"start": v(80.42, -76.68) * mm, "end": v(83.94, -74.96) * mm});
            skLineSegment(sketch, "E329", {"start": v(83.94, -74.96) * mm, "end": v(86.88, -60.03) * mm});
            skLineSegment(sketch, "E330", {"start": v(86.88, -60.03) * mm, "end": v(83.78, -57.22) * mm});
            skLineSegment(sketch, "E331", {"start": v(83.78, -57.22) * mm, "end": v(76.73, -54.37) * mm});
            skLineSegment(sketch, "E332", {"start": v(76.73, -54.37) * mm, "end": v(75.04, -71.08) * mm});
            skLineSegment(sketch, "E333", {"start": v(75.04, -71.08) * mm, "end": v(80.42, -76.68) * mm});
            skLineSegment(sketch, "E334.0", {"start": v(-34.57, -108.65) * mm, "end": v(-34.57, -48.65) * mm});
            skLineSegment(sketch, "E334.1", {"start": v(135.43, -108.65) * mm, "end": v(-34.57, -108.65) * mm});
            skLineSegment(sketch, "E334.2", {"start": v(135.43, -108.65) * mm, "end": v(135.43, -48.65) * mm});
            skLineSegment(sketch, "E334.3", {"start": v(-34.57, -48.65) * mm, "end": v(135.43, -48.65) * mm});
            skLineSegment(sketch, "E335", {"start": v(2.18, -54.71) * mm, "end": v(2.18, -53.65) * mm});
            skSolve(sketch);
        }
        {
            var Q0;
            {var subQ15=sQuery(id+"F0.wireOp",EDGE,"E1");Q0=makeQuery(id+"F0.imprint","IMPRINT",FACE,{"disambiguationData":[TD([[makeQuery(id+"F0.imprint","IMPRINT",EDGE,{"derivedFrom":subQ15}),-1.0]])]});}
            var Q1;
            Q1=makeQuery(id+"F0.imprint","IMPRINT",FACE,{"disambiguationData":[TD([[makeQuery(id+"F0.imprint","IMPRINT",EDGE,{"derivedFrom":sQuery(id+"F0.wireOp",EDGE,"E334.0")}),-1.0]])]});
            extrude(context, id + "F1", {"entities" : qUnion([Q0, Q1]), "depth" : 5 * mm, "offsetDistance" : 25.4 * mm});
        }
    });
